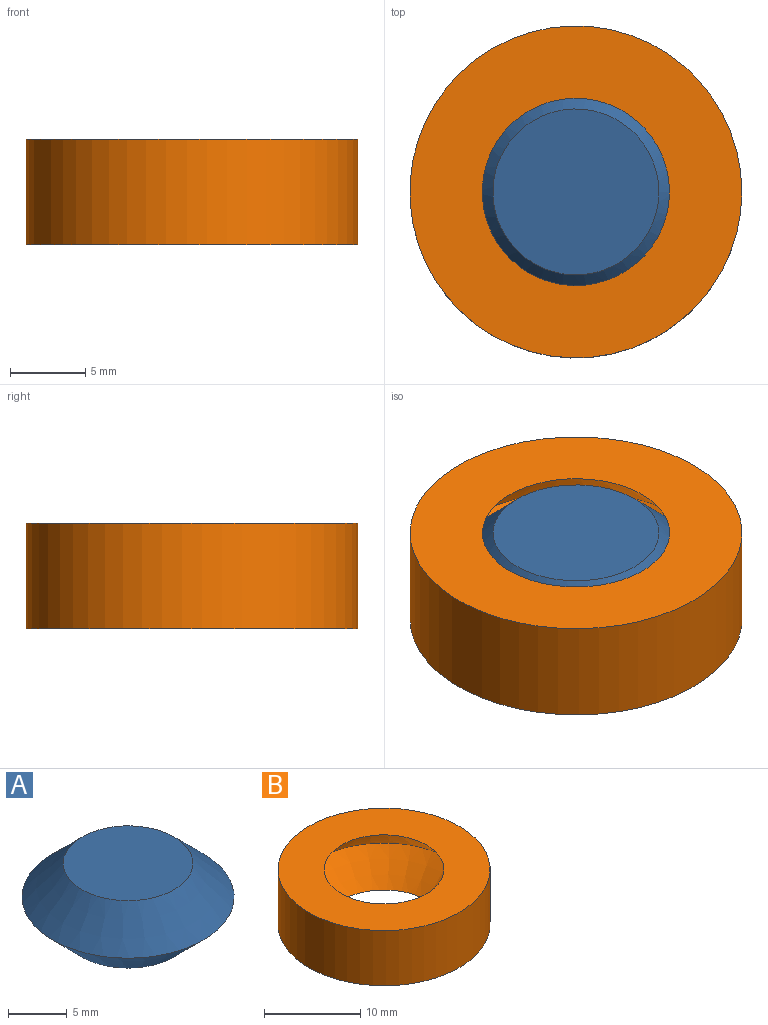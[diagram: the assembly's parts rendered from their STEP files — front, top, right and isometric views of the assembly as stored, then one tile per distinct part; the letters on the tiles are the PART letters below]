
ASSEMBLY  parts=2 mates=1
PART A: 4 faces, bbox 18x18x7 mm
  f0: plane 11x11mm, normal (0,0,-1), area 95mm2, adj f1
  f1: cone r=5.5mm half-angle=45deg, axis (0,0,1), area 225.5mm2, adj f0,f2
  f2: cone r=9mm half-angle=45deg, axis (0,0,-1), area 225.5mm2, adj f1,f3
  f3: plane 11x11mm, normal (0,0,1), area 95mm2, adj f2
PART B: 5 faces, bbox 22x22x7 mm
  f0: plane 22x22mm, normal (0,0,-1), area 259.1mm2, adj f1,f4
  f1: cylinder r=11mm len=22mm, axis (0,0,1), area 483.8mm2, adj f0,f2
  f2: plane 22x22mm, normal (0,0,1), area 259.1mm2, adj f1,f3
  f3: cone r=9.71mm half-angle=45deg, axis (0,0,-1), area 247.5mm2, adj f2,f4
  f4: cone r=6.21mm half-angle=45deg, axis (0,0,1), area 247.5mm2, adj f0,f3
PLACE A t=(-5.39,-3.46,2.68)mm
PLACE B t=(-5.39,-3.46,2.68)mm
MATE revolute A.f1 <-> B.f1  axis (0,0,1) through (-5.39,-3.46,2.68)mm
